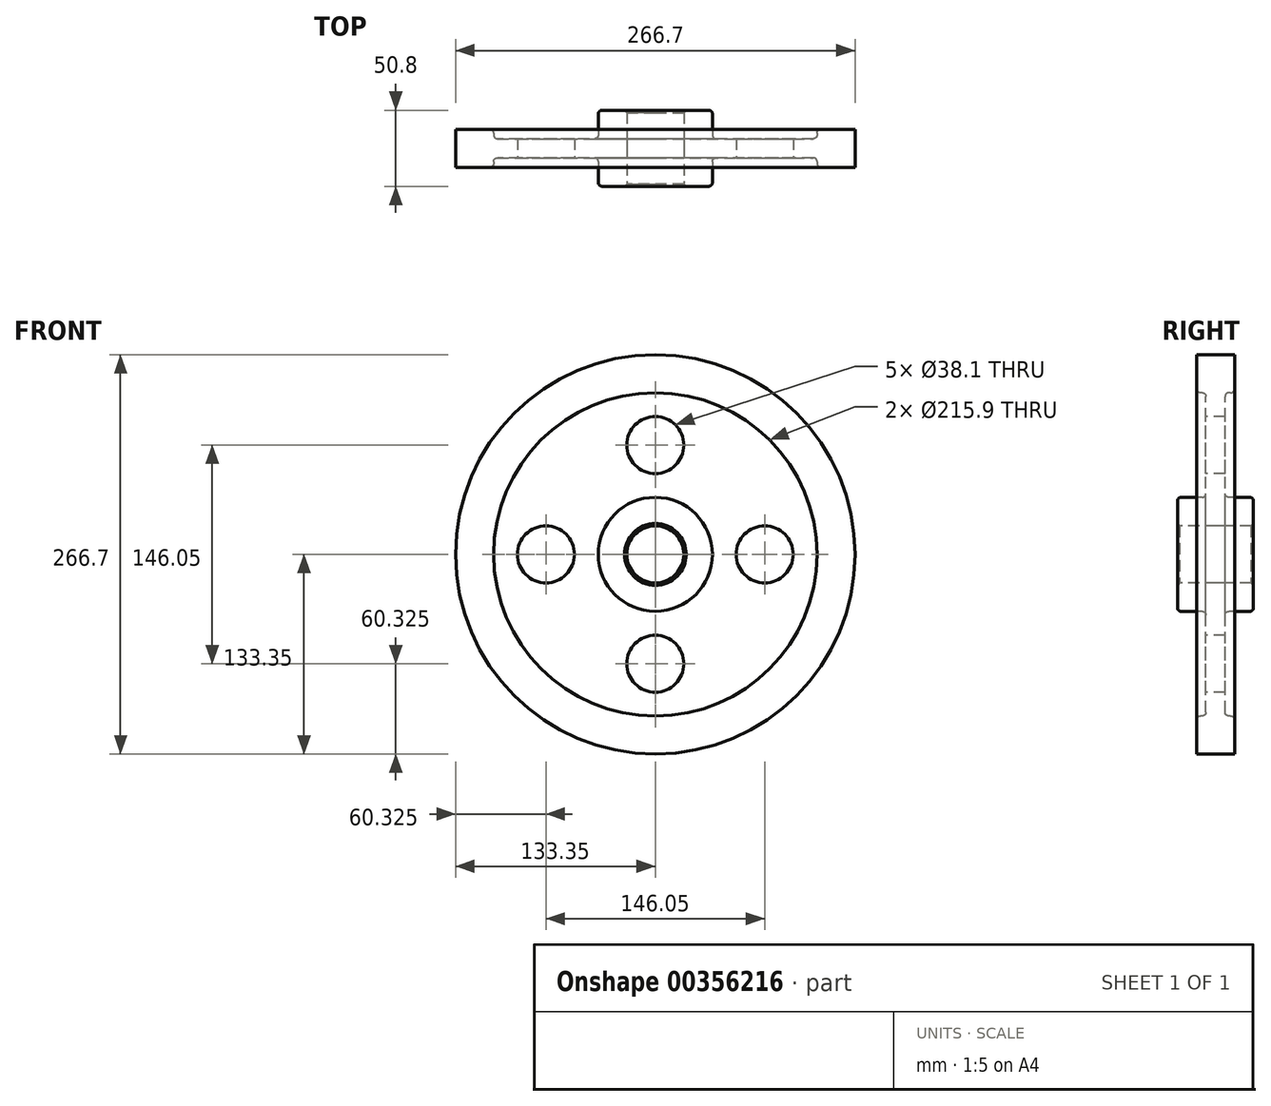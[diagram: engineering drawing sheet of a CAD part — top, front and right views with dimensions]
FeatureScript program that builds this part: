
annotation { "Feature Type Name" : "Feature", "Feature Type Description" : "" }
export const myFeature = defineFeature(function(context is Context, id is Id, definition is map)
    precondition{}
    {
        {
            var Q0;
            Q0=qCreatedBy(makeId("Right.planeOp"),FACE);
            var sketch = newSketch(context, id + "F0", { "sketchPlane" : qUnion([Q0])});
            skLineSegment(sketch, "E0", {"start": v(0, 0) * mm, "end": v(0, 28.58) * mm});
            skLineSegment(sketch, "E1", {"start": v(0, 28.58) * mm, "end": v(0, 73.03) * mm});
            skLineSegment(sketch, "E2", {"start": v(0, 73.03) * mm, "end": v(0, 120.65) * mm});
            skLineSegment(sketch, "E3", {"start": v(0, 0) * mm, "end": v(18.31, 0) * mm});
            skLineSegment(sketch, "E4.bottom", {"start": v(25.4, 38.1) * mm, "end": v(6.35, 38.1) * mm});
            skLineSegment(sketch, "E4.top", {"start": v(25.4, 19.05) * mm, "end": v(-25.4, 19.05) * mm});
            skLineSegment(sketch, "E4.left", {"start": v(25.4, 38.1) * mm, "end": v(25.4, 19.05) * mm});
            skLineSegment(sketch, "E4.right", {"start": v(-25.4, 38.1) * mm, "end": v(-25.4, 19.05) * mm});
            skPoint(sketch, "E4.middle", {"position": v(0, 28.58) * mm});
            skLineSegment(sketch, "E5.bottom", {"start": v(12.7, 107.95) * mm, "end": v(6.35, 107.95) * mm});
            skLineSegment(sketch, "E5.top", {"start": v(12.7, 133.35) * mm, "end": v(-12.7, 133.35) * mm});
            skLineSegment(sketch, "E5.left", {"start": v(12.7, 107.95) * mm, "end": v(12.7, 133.35) * mm});
            skLineSegment(sketch, "E5.right", {"start": v(-12.7, 107.95) * mm, "end": v(-12.7, 133.35) * mm});
            skPoint(sketch, "E5.middle", {"position": v(0, 120.65) * mm});
            skLineSegment(sketch, "E6.left", {"start": v(6.35, 35.03) * mm, "end": v(6.35, 111.02) * mm});
            skLineSegment(sketch, "E6.right", {"start": v(-6.35, 35.03) * mm, "end": v(-6.35, 111.02) * mm});
            skPoint(sketch, "E6.middle", {"position": v(0, 73.03) * mm});
            skLineSegment(sketch, "E7.trimOffspring", {"start": v(-6.35, 107.95) * mm, "end": v(-12.7, 107.95) * mm});
            skLineSegment(sketch, "E8.trimOffspring", {"start": v(-6.35, 38.1) * mm, "end": v(-25.4, 38.1) * mm});
            skSolve(sketch);
        }
        {
            var Q0;
            {var subQ4=sQuery(id+"F0.wireOp",EDGE,"E4.bottom");Q0=makeQuery(id+"F0.imprint","IMPRINT",FACE,{"disambiguationData":[TD([[makeQuery(id+"F0.imprint","IMPRINT",EDGE,{"derivedFrom":subQ4}),1.0]])]});}
            var Q1;
            Q1=sQuery(id+"F0.wireOp",EDGE,"E3");
            revolve(context, id + "F1", {"entities" : qUnion([Q0]), "axis" : qUnion([Q1]), "revolveType" : RevolveType.FULL});
        }
        {
            var Q0;
            Q0=makeQuery(id+"F1.opRevolve","SWEPT_FACE",FACE,{"disambiguationData":[OSD([sQuery(id+"F0.wireOp",EDGE,"E6.right")])]});
            var sketch = newSketch(context, id + "F2", { "sketchPlane" : qUnion([Q0])});
            skLineSegment(sketch, "E9", {"start": v(0, 0) * mm, "end": v(0, 73.03) * mm});
            skCircle(sketch, "E10", {"center": v(0, 73.03) * mm, "radius": 19.05 * mm});
            skCircle(sketch, "E11.1.0", {"center": v(-73.03, 0) * mm, "radius": 19.05 * mm});
            skCircle(sketch, "E11.2.0", {"center": v(0, -73.03) * mm, "radius": 19.05 * mm});
            skCircle(sketch, "E11.3.0", {"center": v(73.03, 0) * mm, "radius": 19.05 * mm});
            skPoint(sketch, "E11.center", {"position": v(0, 0) * mm});
            skSolve(sketch);
        }
        {
            var Q0;
            Q0=makeQuery(id+"F2.imprint","IMPRINT",FACE,{"disambiguationData":[TD([[makeQuery(id+"F2.imprint","IMPRINT",EDGE,{"derivedFrom":sQuery(id+"F2.wireOp",EDGE,"E10")}),1.0]])]});
            var Q1;
            Q1=makeQuery(id+"F2.imprint","IMPRINT",FACE,{"disambiguationData":[TD([[makeQuery(id+"F2.imprint","IMPRINT",EDGE,{"derivedFrom":sQuery(id+"F2.wireOp",EDGE,"E11.3.0")}),1.0]])]});
            var Q2;
            Q2=makeQuery(id+"F2.imprint","IMPRINT",FACE,{"disambiguationData":[TD([[makeQuery(id+"F2.imprint","IMPRINT",EDGE,{"derivedFrom":sQuery(id+"F2.wireOp",EDGE,"E11.2.0")}),1.0]])]});
            var Q3;
            Q3=makeQuery(id+"F2.imprint","IMPRINT",FACE,{"disambiguationData":[TD([[makeQuery(id+"F2.imprint","IMPRINT",EDGE,{"derivedFrom":sQuery(id+"F2.wireOp",EDGE,"E11.1.0")}),1.0]])]});
            extrude(context, id + "F3", {"entities" : qUnion([Q0, Q1, Q2, Q3]), "operationType" : NewBodyOperationType.REMOVE, "oppositeDirection" : true, "depth" : 25.4 * mm});
        }
        {
            var Q0;
            Q0=makeQuery(id+"F1.opRevolve","SWEPT_EDGE",EDGE,{"disambiguationData":[OSD([sQuery(id+"F0.wireOp",EDGE,"E6.right"),sQuery(id+"F0.wireOp",EDGE,"E8.trimOffspring")])]});
            var Q1;
            Q1=makeQuery(id+"F1.opRevolve","SWEPT_EDGE",EDGE,{"disambiguationData":[OSD([sQuery(id+"F0.wireOp",EDGE,"E4.right"),sQuery(id+"F0.wireOp",EDGE,"E8.trimOffspring")])]});
            var Q2;
            Q2=makeQuery(id+"F1.opRevolve","SWEPT_EDGE",EDGE,{"disambiguationData":[OSD([sQuery(id+"F0.wireOp",EDGE,"E6.right"),sQuery(id+"F0.wireOp",EDGE,"E7.trimOffspring")])]});
            var Q3;
            Q3=makeQuery(id+"F1.opRevolve","SWEPT_EDGE",EDGE,{"disambiguationData":[OSD([sQuery(id+"F0.wireOp",EDGE,"E5.right"),sQuery(id+"F0.wireOp",EDGE,"E7.trimOffspring")])]});
            var Q4;
            Q4=makeQuery(id+"F1.opRevolve","SWEPT_EDGE",EDGE,{"disambiguationData":[OSD([sQuery(id+"F0.wireOp",EDGE,"E4.bottom"),sQuery(id+"F0.wireOp",EDGE,"E6.left")])]});
            var Q5;
            Q5=makeQuery(id+"F1.opRevolve","SWEPT_EDGE",EDGE,{"disambiguationData":[OSD([sQuery(id+"F0.wireOp",EDGE,"E4.bottom"),sQuery(id+"F0.wireOp",EDGE,"E4.left")])]});
            var Q6;
            Q6=makeQuery(id+"F1.opRevolve","SWEPT_EDGE",EDGE,{"disambiguationData":[OSD([sQuery(id+"F0.wireOp",EDGE,"E5.bottom"),sQuery(id+"F0.wireOp",EDGE,"E6.left")])]});
            var Q7;
            Q7=makeQuery(id+"F1.opRevolve","SWEPT_EDGE",EDGE,{"disambiguationData":[OSD([sQuery(id+"F0.wireOp",EDGE,"E5.bottom"),sQuery(id+"F0.wireOp",EDGE,"E5.left")])]});
            fillet(context, id + "F4", {"entities" : qUnion([Q0, Q1, Q2, Q3, Q4, Q5, Q6, Q7]), "radius" : 2.54 * mm, "tangentPropagation" : true, "allowEdgeOverflow" : false});
        }
        {
            var Q0;
            Q0=makeQuery(id+"F1.opRevolve","SWEPT_EDGE",EDGE,{"disambiguationData":[OSD([sQuery(id+"F0.wireOp",EDGE,"E4.top"),sQuery(id+"F0.wireOp",EDGE,"E4.right")])]});
            var Q1;
            Q1=makeQuery(id+"F1.opRevolve","SWEPT_EDGE",EDGE,{"disambiguationData":[OSD([sQuery(id+"F0.wireOp",EDGE,"E4.top"),sQuery(id+"F0.wireOp",EDGE,"E4.left")])]});
            chamfer(context, id + "F5", {"entities" : qUnion([Q0, Q1]), "width" : 1.59 * mm, "tangentPropagation" : true});
        }
    });
